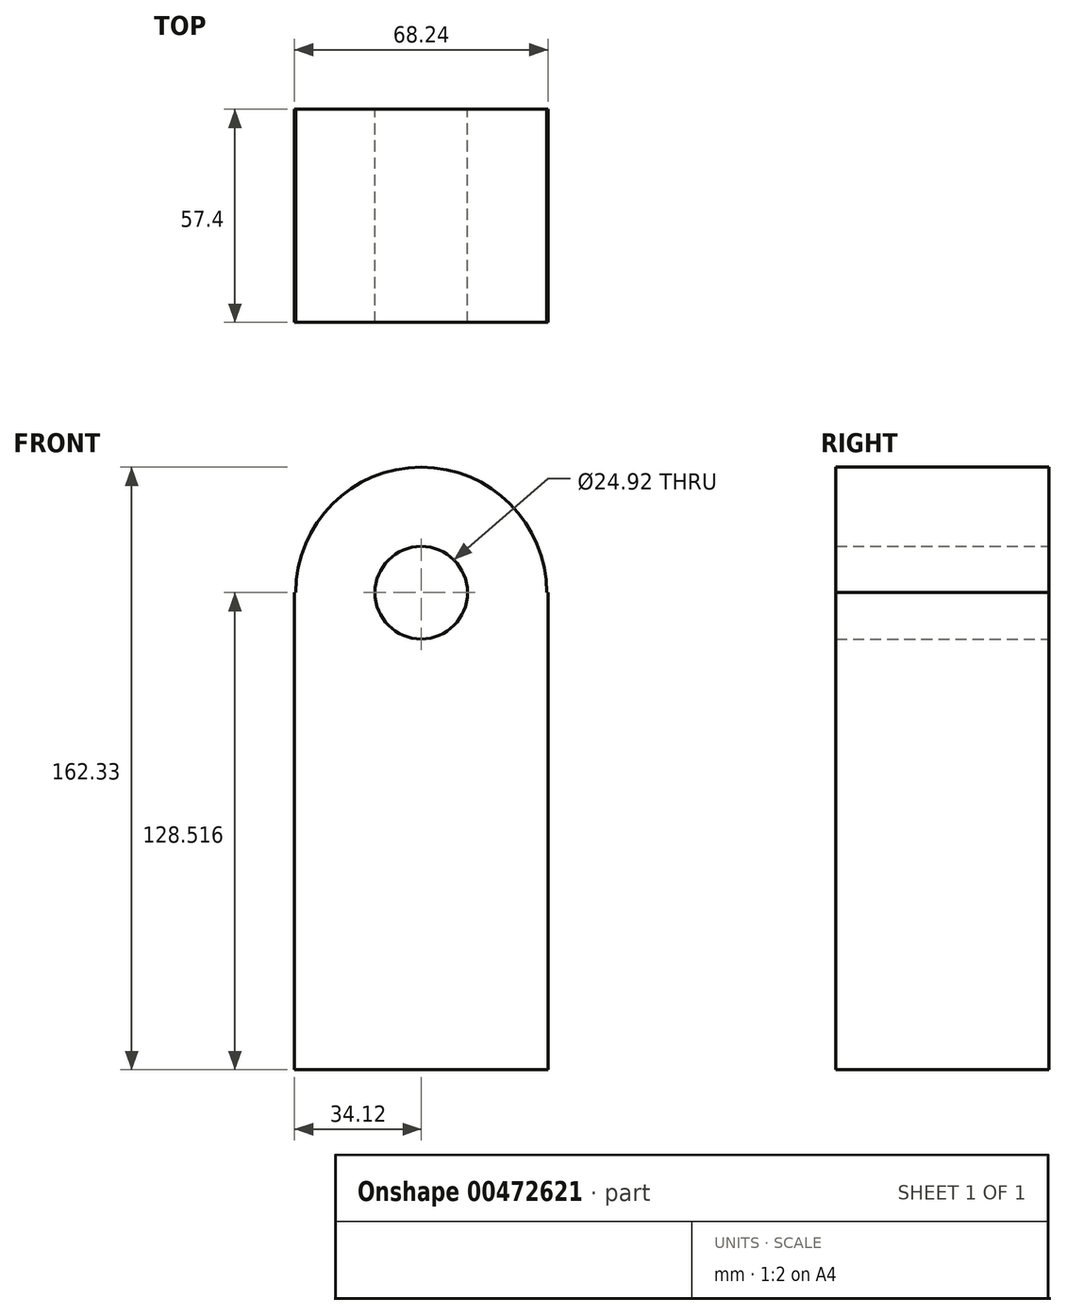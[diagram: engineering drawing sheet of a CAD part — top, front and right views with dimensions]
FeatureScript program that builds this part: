
annotation { "Feature Type Name" : "Feature", "Feature Type Description" : "" }
export const myFeature = defineFeature(function(context is Context, id is Id, definition is map)
    precondition{}
    {
        {
            var Q0;
            Q0=qCreatedBy(makeId("Front.planeOp"),FACE);
            var sketch = newSketch(context, id + "F0", { "sketchPlane" : qUnion([Q0])});
            skLineSegment(sketch, "E0.bottom", {"start": v(34.12, 64.26) * mm, "end": v(33.81, 64.26) * mm});
            skLineSegment(sketch, "E0.top", {"start": v(34.12, -64.26) * mm, "end": v(-34.12, -64.26) * mm});
            skLineSegment(sketch, "E0.left", {"start": v(34.12, 64.26) * mm, "end": v(34.12, -64.26) * mm});
            skLineSegment(sketch, "E0.right", {"start": v(-34.12, 64.26) * mm, "end": v(-34.12, -64.26) * mm});
            skPoint(sketch, "E0.middle", {"position": v(0, 0) * mm});
            skArc(sketch, "E1", {"start": v(33.81, 64.26) * mm, "mid": v(0, 98.07) * mm, "end": v(-33.81, 64.26) * mm});
            skCircle(sketch, "E2", {"center": v(0, 64.26) * mm, "radius": 12.46 * mm});
            skLineSegment(sketch, "E3.trimOffspring", {"start": v(-33.81, 64.26) * mm, "end": v(-34.12, 64.26) * mm});
            skSolve(sketch);
        }
        {
            var Q0;
            Q0=makeQuery(id+"F0.imprint","IMPRINT",FACE,{"disambiguationData":[TD([[makeQuery(id+"F0.imprint","IMPRINT",EDGE,{"derivedFrom":sQuery(id+"F0.wireOp",EDGE,"E0.bottom")}),1.0]])]});
            extrude(context, id + "F1", {"entities" : qUnion([Q0]), "depth" : 57.4 * mm});
        }
    });
